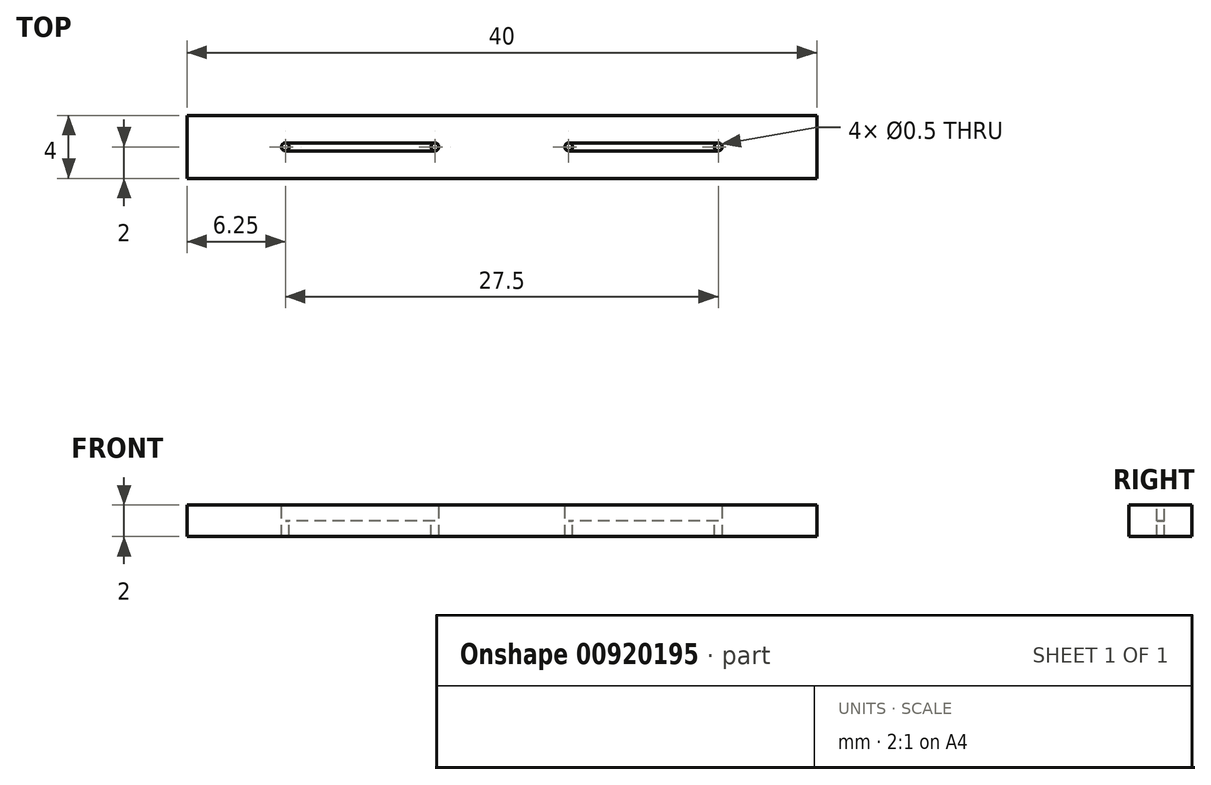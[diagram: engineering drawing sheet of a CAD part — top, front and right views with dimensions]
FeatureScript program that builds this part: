
annotation { "Feature Type Name" : "Feature", "Feature Type Description" : "" }
export const myFeature = defineFeature(function(context is Context, id is Id, definition is map)
    precondition{}
    {
        {
            var Q0;
            Q0=qCreatedBy(makeId("Top.planeOp"),FACE);
            var sketch = newSketch(context, id + "F0", { "sketchPlane" : qUnion([Q0])});
            skLineSegment(sketch, "E0.bottom", {"start": v(-20, 2) * mm, "end": v(20, 2) * mm});
            skLineSegment(sketch, "E0.top", {"start": v(-20, -2) * mm, "end": v(20, -2) * mm});
            skLineSegment(sketch, "E0.left", {"start": v(-20, 2) * mm, "end": v(-20, -2) * mm});
            skLineSegment(sketch, "E0.right", {"start": v(20, 2) * mm, "end": v(20, -2) * mm});
            skSolve(sketch);
        }
        {
            var Q0;
            Q0=makeQuery(id+"F0.imprint","IMPRINT",FACE,{"disambiguationData":[TD([[makeQuery(id+"F0.imprint","IMPRINT",EDGE,{"derivedFrom":sQuery(id+"F0.wireOp",EDGE,"E0.bottom")}),-1.0]])]});
            extrude(context, id + "F1", {"entities" : qUnion([Q0]), "depth" : 2 * mm, "offsetDistance" : 25 * mm});
        }
        {
            var Q0;
            Q0=makeQuery(id+"F1.opExtrude","CAP_FACE",FACE,{"disambiguationData":[OSD([sQuery(id+"F0.wireOp",EDGE,"E0.bottom"),sQuery(id+"F0.wireOp",EDGE,"E0.top"),sQuery(id+"F0.wireOp",EDGE,"E0.left"),sQuery(id+"F0.wireOp",EDGE,"E0.right")])],"isStart":false});
            var sketch = newSketch(context, id + "F2", { "sketchPlane" : qUnion([Q0])});
            skLineSegment(sketch, "E1.bottom", {"start": v(-4, -0.25) * mm, "end": v(-14, -0.25) * mm});
            skLineSegment(sketch, "E1.top", {"start": v(-4, 0.25) * mm, "end": v(-14, 0.25) * mm});
            skLineSegment(sketch, "E1.left", {"start": v(-4, -0.25) * mm, "end": v(-4, 0.25) * mm});
            skLineSegment(sketch, "E1.right", {"start": v(-14, -0.25) * mm, "end": v(-14, 0.25) * mm});
            skPoint(sketch, "E1.middle", {"position": v(-9, 0) * mm});
            skLineSegment(sketch, "E2.bottom", {"start": v(14, -0.25) * mm, "end": v(4, -0.25) * mm});
            skLineSegment(sketch, "E2.top", {"start": v(14, 0.25) * mm, "end": v(4, 0.25) * mm});
            skLineSegment(sketch, "E2.left", {"start": v(14, -0.25) * mm, "end": v(14, 0.25) * mm});
            skLineSegment(sketch, "E2.right", {"start": v(4, -0.25) * mm, "end": v(4, 0.25) * mm});
            skPoint(sketch, "E2.middle", {"position": v(9, 0) * mm});
            skSolve(sketch);
        }
        {
            var Q0;
            Q0=makeQuery(id+"F2.imprint","IMPRINT",FACE,{"disambiguationData":[TD([[makeQuery(id+"F2.imprint","IMPRINT",EDGE,{"derivedFrom":sQuery(id+"F2.wireOp",EDGE,"E1.bottom")}),-1.0]])]});
            var Q1;
            Q1=makeQuery(id+"F2.imprint","IMPRINT",FACE,{"disambiguationData":[TD([[makeQuery(id+"F2.imprint","IMPRINT",EDGE,{"derivedFrom":sQuery(id+"F2.wireOp",EDGE,"E2.bottom")}),-1.0]])]});
            extrude(context, id + "F3", {"entities" : qUnion([Q0, Q1]), "operationType" : NewBodyOperationType.REMOVE, "oppositeDirection" : true, "depth" : 1 * mm, "offsetDistance" : 25 * mm});
        }
        {
            var Q0;
            Q0=makeQuery(id+"F3.boolean.opBoolean","COPY",FACE,{"derivedFrom":makeQuery(id+"F3.opExtrude","CAP_FACE",FACE,{"disambiguationData":[OSD([sQuery(id+"F2.wireOp",EDGE,"E1.bottom"),sQuery(id+"F2.wireOp",EDGE,"E1.top"),sQuery(id+"F2.wireOp",EDGE,"E1.left"),sQuery(id+"F2.wireOp",EDGE,"E1.right")])],"isStart":false})});
            var sketch = newSketch(context, id + "F4", { "sketchPlane" : qUnion([Q0])});
            skCircle(sketch, "E3", {"center": v(-13.75, 0) * mm, "radius": 0.25 * mm});
            skCircle(sketch, "E4", {"center": v(-4.25, 0) * mm, "radius": 0.25 * mm});
            skCircle(sketch, "E5", {"center": v(4.25, 0) * mm, "radius": 0.25 * mm});
            skCircle(sketch, "E6", {"center": v(13.75, 0) * mm, "radius": 0.25 * mm});
            skSolve(sketch);
        }
        {
            var Q0;
            {var subQ0=sQuery(id+"F4.wireOp",EDGE,"E3");var subQ1=makeQuery(id+"F4.imprint","INTERSECT",VERTEX,{"derivedFrom":[makeQuery(id+"F3.boolean.opBoolean","COPY",EDGE,{"derivedFrom":makeQuery(id+"F3.opExtrude","CAP_EDGE",EDGE,{"disambiguationData":[OSD([sQuery(id+"F2.wireOp",EDGE,"E1.right")])],"isStart":false})}),subQ0]});Q0=makeQuery(id+"F4.imprint","IMPRINT",FACE,{"disambiguationData":[TD([[makeQuery(id+"F4.imprint","IMPRINT",EDGE,{"disambiguationData":[TD([[subQ1,1.0]])],"derivedFrom":subQ0}),1.0]])]});}
            var Q1;
            {var subQ0=sQuery(id+"F4.wireOp",EDGE,"E4");var subQ1=makeQuery(id+"F4.imprint","INTERSECT",VERTEX,{"derivedFrom":[makeQuery(id+"F3.boolean.opBoolean","COPY",EDGE,{"derivedFrom":makeQuery(id+"F3.opExtrude","CAP_EDGE",EDGE,{"disambiguationData":[OSD([sQuery(id+"F2.wireOp",EDGE,"E1.top")])],"isStart":false})}),subQ0]});Q1=makeQuery(id+"F4.imprint","IMPRINT",FACE,{"disambiguationData":[TD([[makeQuery(id+"F4.imprint","IMPRINT",EDGE,{"disambiguationData":[TD([[subQ1,1.0]])],"derivedFrom":subQ0}),1.0]])]});}
            var Q2;
            Q2=makeQuery(id+"F4.imprint","IMPRINT",FACE,{"disambiguationData":[TD([[makeQuery(id+"F4.imprint","IMPRINT",EDGE,{"derivedFrom":sQuery(id+"F4.wireOp",EDGE,"E6")}),1.0]])]});
            var Q3;
            Q3=makeQuery(id+"F4.imprint","IMPRINT",FACE,{"disambiguationData":[TD([[makeQuery(id+"F4.imprint","IMPRINT",EDGE,{"derivedFrom":sQuery(id+"F4.wireOp",EDGE,"E5")}),1.0]])]});
            extrude(context, id + "F5", {"entities" : qUnion([Q0, Q1, Q2, Q3]), "operationType" : NewBodyOperationType.REMOVE, "oppositeDirection" : true, "depth" : 25 * mm, "offsetDistance" : 25 * mm});
        }
        {
            var Q0;
            Q0=makeQuery(id+"F3.boolean.opBoolean","COPY",EDGE,{"derivedFrom":makeQuery(id+"F3.opExtrude","SWEPT_EDGE",EDGE,{"disambiguationData":[OSD([sQuery(id+"F2.wireOp",EDGE,"E2.top"),sQuery(id+"F2.wireOp",EDGE,"E2.left")])]})});
            var Q1;
            Q1=makeQuery(id+"F3.boolean.opBoolean","COPY",EDGE,{"derivedFrom":makeQuery(id+"F3.opExtrude","SWEPT_EDGE",EDGE,{"disambiguationData":[OSD([sQuery(id+"F2.wireOp",EDGE,"E2.bottom"),sQuery(id+"F2.wireOp",EDGE,"E2.left")])]})});
            var Q2;
            Q2=makeQuery(id+"F3.boolean.opBoolean","COPY",EDGE,{"derivedFrom":makeQuery(id+"F3.opExtrude","SWEPT_EDGE",EDGE,{"disambiguationData":[OSD([sQuery(id+"F2.wireOp",EDGE,"E2.bottom"),sQuery(id+"F2.wireOp",EDGE,"E2.right")])]})});
            var Q3;
            Q3=makeQuery(id+"F3.boolean.opBoolean","COPY",EDGE,{"derivedFrom":makeQuery(id+"F3.opExtrude","SWEPT_EDGE",EDGE,{"disambiguationData":[OSD([sQuery(id+"F2.wireOp",EDGE,"E2.top"),sQuery(id+"F2.wireOp",EDGE,"E2.right")])]})});
            var Q4;
            Q4=makeQuery(id+"F3.boolean.opBoolean","COPY",EDGE,{"derivedFrom":makeQuery(id+"F3.opExtrude","SWEPT_EDGE",EDGE,{"disambiguationData":[OSD([sQuery(id+"F2.wireOp",EDGE,"E1.top"),sQuery(id+"F2.wireOp",EDGE,"E1.right")])]})});
            var Q5;
            Q5=makeQuery(id+"F3.boolean.opBoolean","COPY",EDGE,{"derivedFrom":makeQuery(id+"F3.opExtrude","SWEPT_EDGE",EDGE,{"disambiguationData":[OSD([sQuery(id+"F2.wireOp",EDGE,"E1.bottom"),sQuery(id+"F2.wireOp",EDGE,"E1.right")])]})});
            var Q6;
            Q6=makeQuery(id+"F3.boolean.opBoolean","COPY",EDGE,{"derivedFrom":makeQuery(id+"F3.opExtrude","SWEPT_EDGE",EDGE,{"disambiguationData":[OSD([sQuery(id+"F2.wireOp",EDGE,"E1.top"),sQuery(id+"F2.wireOp",EDGE,"E1.left")])]})});
            var Q7;
            Q7=makeQuery(id+"F3.boolean.opBoolean","COPY",EDGE,{"derivedFrom":makeQuery(id+"F3.opExtrude","SWEPT_EDGE",EDGE,{"disambiguationData":[OSD([sQuery(id+"F2.wireOp",EDGE,"E1.bottom"),sQuery(id+"F2.wireOp",EDGE,"E1.left")])]})});
            fillet(context, id + "F6", {"entities" : qUnion([Q0, Q1, Q2, Q3, Q4, Q5, Q6, Q7]), "radius" : 0.25 * mm, "tangentPropagation" : true, "allowEdgeOverflow" : false});
        }
    });
